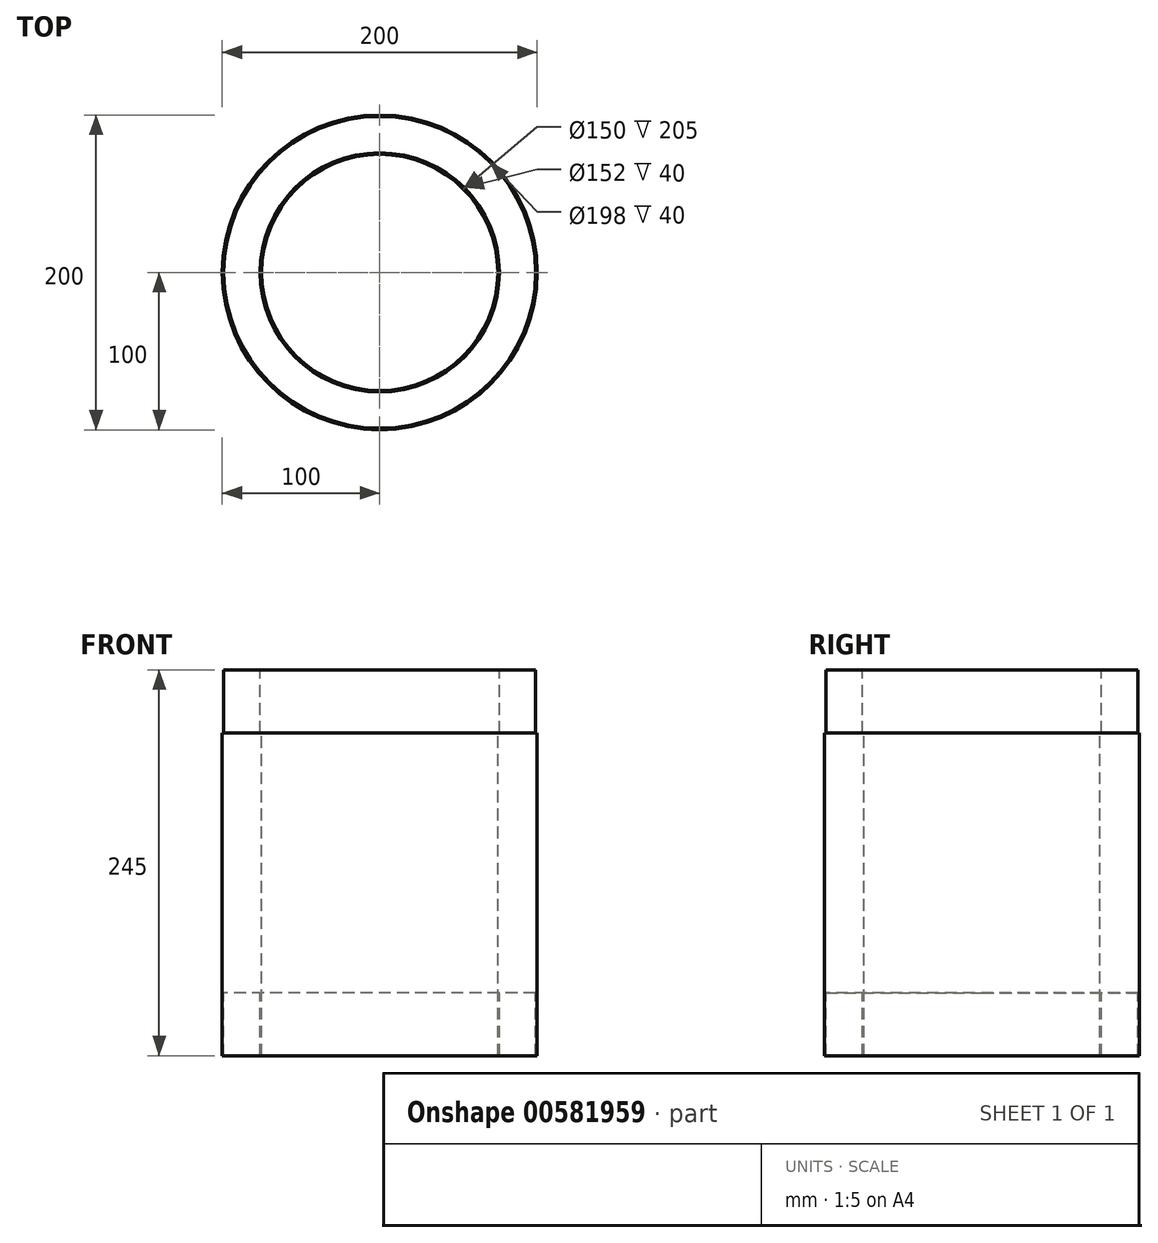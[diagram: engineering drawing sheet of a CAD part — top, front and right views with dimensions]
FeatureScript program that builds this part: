
annotation { "Feature Type Name" : "Feature", "Feature Type Description" : "" }
export const myFeature = defineFeature(function(context is Context, id is Id, definition is map)
    precondition{}
    {
        {
            var Q0;
            Q0=qCreatedBy(makeId("Front.planeOp"),FACE);
            var sketch = newSketch(context, id + "F0", { "sketchPlane" : qUnion([Q0])});
            skLineSegment(sketch, "E0", {"start": v(0, 345.75) * mm, "end": v(0, -558.03) * mm, "construction": true});
            skLineSegment(sketch, "E1", {"start": v(-75, -518.84) * mm, "end": v(-75, -313.84) * mm});
            skLineSegment(sketch, "E2", {"start": v(-75, -313.84) * mm, "end": v(-76, -313.84) * mm});
            skLineSegment(sketch, "E3", {"start": v(-76, -313.84) * mm, "end": v(-76, -273.84) * mm});
            skLineSegment(sketch, "E4", {"start": v(-76, -273.84) * mm, "end": v(-99, -273.84) * mm});
            skLineSegment(sketch, "E5", {"start": v(-99, -273.84) * mm, "end": v(-99, -313.84) * mm});
            skLineSegment(sketch, "E6", {"start": v(-99, -313.84) * mm, "end": v(-100, -313.84) * mm});
            skLineSegment(sketch, "E7", {"start": v(-100, -313.84) * mm, "end": v(-100, -518.84) * mm});
            skLineSegment(sketch, "E8", {"start": v(-100, -518.84) * mm, "end": v(-99, -518.84) * mm});
            skLineSegment(sketch, "E9", {"start": v(-99, -518.84) * mm, "end": v(-99, -478.84) * mm});
            skLineSegment(sketch, "E10", {"start": v(-99, -478.84) * mm, "end": v(-76, -478.84) * mm});
            skLineSegment(sketch, "E11", {"start": v(-76, -478.84) * mm, "end": v(-76, -518.84) * mm});
            skLineSegment(sketch, "E12", {"start": v(-76, -518.84) * mm, "end": v(-75, -518.84) * mm});
            skSolve(sketch);
        }
        {
            var Q0;
            Q0=qSketchRegion(id+"F0",true);
            var Q1;
            Q1=sQuery(id+"F0.wireOp",EDGE,"E0");
            revolve(context, id + "F1", {"entities" : qUnion([Q0]), "axis" : qUnion([Q1]), "revolveType" : RevolveType.FULL});
        }
    });
